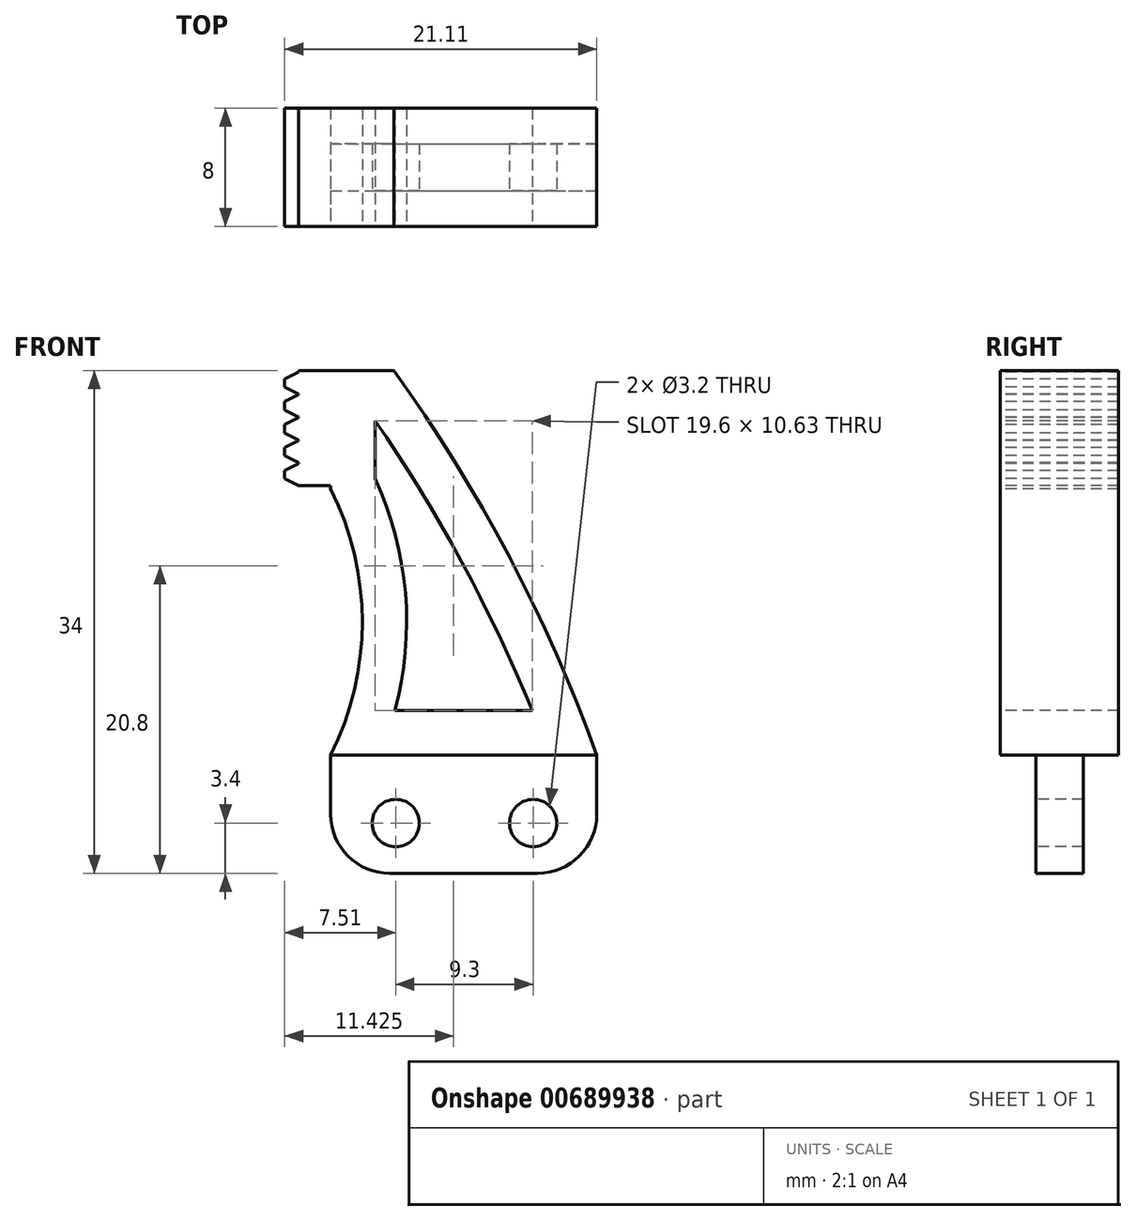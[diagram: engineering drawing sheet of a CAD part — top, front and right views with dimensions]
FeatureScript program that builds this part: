
annotation { "Feature Type Name" : "Feature", "Feature Type Description" : "" }
export const myFeature = defineFeature(function(context is Context, id is Id, definition is map)
    precondition{}
    {
        {
            var Q0;
            Q0=qCreatedBy(makeId("Front.planeOp"),FACE);
            var sketch = newSketch(context, id + "F0", { "sketchPlane" : qUnion([Q0])});
            skLineSegment(sketch, "E0.bottom", {"start": v(9, 15) * mm, "end": v(-9, 15) * mm});
            skLineSegment(sketch, "E0.left", {"start": v(9, 15) * mm, "end": v(9, -15) * mm});
            skLineSegment(sketch, "E0.right", {"start": v(-9, 15) * mm, "end": v(-9, -15) * mm});
            skPoint(sketch, "E0.middle", {"position": v(0, 0) * mm});
            skArc(sketch, "E1", {"start": v(-9, -11) * mm, "mid": v(-6.86, -2) * mm, "end": v(-9, 7) * mm});
            skArc(sketch, "E2", {"start": v(9, -11) * mm, "mid": v(3.04, 2.48) * mm, "end": v(-4.73, 15) * mm});
            skLineSegment(sketch, "E3", {"start": v(-11.16, 14.92) * mm, "end": v(-12.66, 14.17) * mm});
            skLineSegment(sketch, "E4", {"start": v(-11.16, 13.42) * mm, "end": v(-12.66, 14.17) * mm});
            skLineSegment(sketch, "E5.1.0.1", {"start": v(-11.16, 11.87) * mm, "end": v(-12.66, 12.62) * mm});
            skLineSegment(sketch, "E5.1.0.2", {"start": v(-11.16, 13.37) * mm, "end": v(-12.66, 12.62) * mm});
            skLineSegment(sketch, "E5.2.0.1", {"start": v(-11.16, 10.32) * mm, "end": v(-12.66, 11.07) * mm});
            skLineSegment(sketch, "E5.2.0.2", {"start": v(-11.16, 11.82) * mm, "end": v(-12.66, 11.07) * mm});
            skLineSegment(sketch, "E5.3.0.1", {"start": v(-11.16, 8.77) * mm, "end": v(-12.66, 9.52) * mm});
            skLineSegment(sketch, "E5.3.0.2", {"start": v(-11.16, 10.27) * mm, "end": v(-12.66, 9.52) * mm});
            skLineSegment(sketch, "E5.4.0.1", {"start": v(-11.16, 7.22) * mm, "end": v(-12.66, 7.97) * mm});
            skLineSegment(sketch, "E5.4.0.2", {"start": v(-11.16, 8.72) * mm, "end": v(-12.66, 7.97) * mm});
            skLineSegment(sketch, "E6", {"start": v(-9, -11) * mm, "end": v(9, -11) * mm});
            skLineSegment(sketch, "E7.top", {"start": v(-9, -19) * mm, "end": v(9, -19) * mm});
            skLineSegment(sketch, "E7.left", {"start": v(-9, -15) * mm, "end": v(-9, -19) * mm});
            skLineSegment(sketch, "E7.right", {"start": v(9, -15) * mm, "end": v(9, -19) * mm});
            skLineSegment(sketch, "E8.bottom", {"start": v(-9, 15) * mm, "end": v(-11.16, 15) * mm});
            skLineSegment(sketch, "E8.left", {"start": v(-9, 15) * mm, "end": v(-9, 7.22) * mm});
            skLineSegment(sketch, "E8.right", {"start": v(-11.16, 15) * mm, "end": v(-11.16, 7.22) * mm});
            skLineSegment(sketch, "E9.bottom", {"start": v(-9, 7) * mm, "end": v(-11.16, 7) * mm});
            skLineSegment(sketch, "E9.left", {"start": v(-9, 7) * mm, "end": v(-9, 7.22) * mm});
            skLineSegment(sketch, "E9.right", {"start": v(-11.16, 7) * mm, "end": v(-11.16, 7.22) * mm});
            skLineSegment(sketch, "E10", {"start": v(-11.16, 7.22) * mm, "end": v(-9, 7.22) * mm});
            skLineSegment(sketch, "E11", {"start": v(-12.11, 14.44) * mm, "end": v(-12.11, 7.7) * mm});
            skSolve(sketch);
        }
        {
            var Q0;
            {var subQ0=sQuery(id+"F0.wireOp",EDGE,"E11");var subQ1=sQuery(id+"F0.wireOp",EDGE,"E3");var subQ2=makeQuery(id+"F0.imprint","INTERSECT",VERTEX,{"derivedFrom":[subQ1,subQ0]});Q0=makeQuery(id+"F0.imprint","IMPRINT",FACE,{"disambiguationData":[TD([[makeQuery(id+"F0.imprint","IMPRINT",EDGE,{"disambiguationData":[TD([[subQ2,1.0]])],"derivedFrom":subQ1}),1.0]])]});}
            var Q1;
            {var subQ0=sQuery(id+"F0.wireOp",EDGE,"E11");var subQ1=sQuery(id+"F0.wireOp",EDGE,"E5.1.0.1");var subQ2=makeQuery(id+"F0.imprint","INTERSECT",VERTEX,{"derivedFrom":[subQ1,subQ0]});Q1=makeQuery(id+"F0.imprint","IMPRINT",FACE,{"disambiguationData":[TD([[makeQuery(id+"F0.imprint","IMPRINT",EDGE,{"disambiguationData":[TD([[subQ2,1.0]])],"derivedFrom":subQ1}),-1.0]])]});}
            var Q2;
            {var subQ8=sQuery(id+"F0.wireOp",EDGE,"E8.bottom");Q2=makeQuery(id+"F0.imprint","IMPRINT",FACE,{"disambiguationData":[TD([[makeQuery(id+"F0.imprint","IMPRINT",EDGE,{"derivedFrom":subQ8}),1.0]])]});}
            var Q3;
            Q3=makeQuery(id+"F0.imprint","IMPRINT",FACE,{"disambiguationData":[TD([[makeQuery(id+"F0.imprint","IMPRINT",EDGE,{"derivedFrom":sQuery(id+"F0.wireOp",EDGE,"E1")}),-1.0]])]});
            var Q4;
            {var subQ0=sQuery(id+"F0.wireOp",EDGE,"E11");var subQ1=sQuery(id+"F0.wireOp",EDGE,"E5.2.0.1");var subQ2=makeQuery(id+"F0.imprint","INTERSECT",VERTEX,{"derivedFrom":[subQ1,subQ0]});Q4=makeQuery(id+"F0.imprint","IMPRINT",FACE,{"disambiguationData":[TD([[makeQuery(id+"F0.imprint","IMPRINT",EDGE,{"disambiguationData":[TD([[subQ2,1.0]])],"derivedFrom":subQ1}),-1.0]])]});}
            var Q5;
            {var subQ0=sQuery(id+"F0.wireOp",EDGE,"E11");var subQ1=sQuery(id+"F0.wireOp",EDGE,"E5.3.0.1");var subQ2=makeQuery(id+"F0.imprint","INTERSECT",VERTEX,{"derivedFrom":[subQ1,subQ0]});Q5=makeQuery(id+"F0.imprint","IMPRINT",FACE,{"disambiguationData":[TD([[makeQuery(id+"F0.imprint","IMPRINT",EDGE,{"disambiguationData":[TD([[subQ2,1.0]])],"derivedFrom":subQ1}),-1.0]])]});}
            var Q6;
            {var subQ3=sQuery(id+"F0.wireOp",EDGE,"E11");var subQ5=sQuery(id+"F0.wireOp",EDGE,"E5.4.0.2");var subQ6=makeQuery(id+"F0.imprint","INTERSECT",VERTEX,{"derivedFrom":[subQ5,subQ3]});Q6=makeQuery(id+"F0.imprint","IMPRINT",FACE,{"disambiguationData":[TD([[makeQuery(id+"F0.imprint","IMPRINT",EDGE,{"disambiguationData":[TD([[subQ6,1.0]])],"derivedFrom":subQ5}),1.0]])]});}
            var Q7;
            {var subQ2=sQuery(id+"F0.wireOp",EDGE,"E6");Q7=makeQuery(id+"F0.imprint","IMPRINT",FACE,{"disambiguationData":[TD([[makeQuery(id+"F0.imprint","IMPRINT",EDGE,{"derivedFrom":subQ2}),-1.0]])]});}
            extrude(context, id + "F1", {"entities" : qUnion([Q0, Q1, Q2, Q3, Q4, Q5, Q6, Q7]), "oppositeDirection" : true, "depth" : 8 * mm, "offsetDistance" : 25 * mm});
        }
        {
            var Q0;
            Q0=makeQuery(id+"F1.opExtrude","CAP_FACE",FACE,{"disambiguationData":[OSD([sQuery(id+"F0.wireOp",EDGE,"E0.bottom"),sQuery(id+"F0.wireOp",EDGE,"E0.left"),sQuery(id+"F0.wireOp",EDGE,"E0.right"),sQuery(id+"F0.wireOp",EDGE,"E1"),sQuery(id+"F0.wireOp",EDGE,"E2"),sQuery(id+"F0.wireOp",EDGE,"E3"),sQuery(id+"F0.wireOp",EDGE,"E4"),sQuery(id+"F0.wireOp",EDGE,"E5.1.0.1"),sQuery(id+"F0.wireOp",EDGE,"E5.1.0.2"),sQuery(id+"F0.wireOp",EDGE,"E5.2.0.1"),sQuery(id+"F0.wireOp",EDGE,"E5.2.0.2"),sQuery(id+"F0.wireOp",EDGE,"E5.3.0.1"),sQuery(id+"F0.wireOp",EDGE,"E5.3.0.2"),sQuery(id+"F0.wireOp",EDGE,"E5.4.0.1"),sQuery(id+"F0.wireOp",EDGE,"E5.4.0.2"),sQuery(id+"F0.wireOp",EDGE,"ii1cAA1e-JSJr-z0bZ-yPhd-YXalWYOk9meH"),sQuery(id+"F0.wireOp",EDGE,"NeUnMBCx-EcG5-3TzF-d2Iy-VHdHwbOGnCjQ"),sQuery(id+"F0.wireOp",EDGE,"Bu8GrmuG-hVLc-6Zwb-ZN9j-FqlKQepw3AUV"),sQuery(id+"F0.wireOp",EDGE,"PhBtE8ru-nsp9-KEh6-Witq-BTG184TXn8xR"),sQuery(id+"F0.wireOp",EDGE,"dVbz5flj-GqEQ-BWn1-bWRb-yC5Nv96dNbSN"),sQuery(id+"F0.wireOp",EDGE,"E7.top"),sQuery(id+"F0.wireOp",EDGE,"E7.left"),sQuery(id+"F0.wireOp",EDGE,"E7.right")])],"isStart":false});
            var sketch = newSketch(context, id + "F2", { "sketchPlane" : qUnion([Q0])});
            skLineSegment(sketch, "E12", {"start": v(9, -11) * mm, "end": v(-9, -11) * mm});
            skSolve(sketch);
        }
        {
            var Q0;
            {var subQ2=sQuery(id+"F0.wireOp",EDGE,"E6");Q0=makeQuery(id+"F0.imprint","IMPRINT",FACE,{"disambiguationData":[TD([[makeQuery(id+"F0.imprint","IMPRINT",EDGE,{"derivedFrom":subQ2}),-1.0]])]});}
            extrude(context, id + "F3", {"entities" : qUnion([Q0]), "operationType" : NewBodyOperationType.REMOVE, "oppositeDirection" : true, "depth" : 2.4 * mm, "offsetDistance" : 25 * mm});
        }
        {
            var Q0;
            Q0=makeQuery(id+"F1.opExtrude","CAP_FACE",FACE,{"disambiguationData":[OSD([sQuery(id+"F0.wireOp",EDGE,"E0.bottom"),sQuery(id+"F0.wireOp",EDGE,"E0.left"),sQuery(id+"F0.wireOp",EDGE,"E0.right"),sQuery(id+"F0.wireOp",EDGE,"E1"),sQuery(id+"F0.wireOp",EDGE,"E2"),sQuery(id+"F0.wireOp",EDGE,"E3"),sQuery(id+"F0.wireOp",EDGE,"E4"),sQuery(id+"F0.wireOp",EDGE,"E5.1.0.1"),sQuery(id+"F0.wireOp",EDGE,"E5.1.0.2"),sQuery(id+"F0.wireOp",EDGE,"E5.2.0.1"),sQuery(id+"F0.wireOp",EDGE,"E5.2.0.2"),sQuery(id+"F0.wireOp",EDGE,"E5.3.0.1"),sQuery(id+"F0.wireOp",EDGE,"E5.3.0.2"),sQuery(id+"F0.wireOp",EDGE,"E5.4.0.1"),sQuery(id+"F0.wireOp",EDGE,"E5.4.0.2"),sQuery(id+"F0.wireOp",EDGE,"ii1cAA1e-JSJr-z0bZ-yPhd-YXalWYOk9meH"),sQuery(id+"F0.wireOp",EDGE,"NeUnMBCx-EcG5-3TzF-d2Iy-VHdHwbOGnCjQ"),sQuery(id+"F0.wireOp",EDGE,"Bu8GrmuG-hVLc-6Zwb-ZN9j-FqlKQepw3AUV"),sQuery(id+"F0.wireOp",EDGE,"PhBtE8ru-nsp9-KEh6-Witq-BTG184TXn8xR"),sQuery(id+"F0.wireOp",EDGE,"dVbz5flj-GqEQ-BWn1-bWRb-yC5Nv96dNbSN"),sQuery(id+"F0.wireOp",EDGE,"E7.top"),sQuery(id+"F0.wireOp",EDGE,"E7.left"),sQuery(id+"F0.wireOp",EDGE,"E7.right")])],"isStart":true});
            var sketch = newSketch(context, id + "F4", { "sketchPlane" : qUnion([Q0])});
            skLineSegment(sketch, "E13", {"start": v(-9, -11) * mm, "end": v(9, -11) * mm});
            skSolve(sketch);
        }
        {
            var Q0;
            Q0=makeQuery(id+"F2.imprint","IMPRINT",FACE,{"disambiguationData":[TD([[makeQuery(id+"F2.imprint","IMPRINT",EDGE,{"derivedFrom":sQuery(id+"F2.wireOp",EDGE,"E12")}),1.0]])]});
            extrude(context, id + "F5", {"entities" : qUnion([Q0]), "operationType" : NewBodyOperationType.REMOVE, "oppositeDirection" : true, "depth" : 2.4 * mm, "offsetDistance" : 25 * mm});
        }
        {
            var Q0;
            Q0=makeQuery(id+"F4.imprint","IMPRINT",FACE,{"disambiguationData":[TD([[makeQuery(id+"F4.imprint","IMPRINT",EDGE,{"derivedFrom":sQuery(id+"F4.wireOp",EDGE,"E13")}),1.0]])]});
            var sketch = newSketch(context, id + "F6", { "sketchPlane" : qUnion([Q0])});
            skArc(sketch, "E14.0", {"start": v(-9, -11) * mm, "mid": v(-6.86, -2) * mm, "end": v(-9, 7) * mm});
            skArc(sketch, "E15.0", {"start": v(9, -11) * mm, "mid": v(3.04, 2.48) * mm, "end": v(-4.73, 15) * mm});
            skLineSegment(sketch, "E16.0", {"start": v(-9, -11) * mm, "end": v(9, -11) * mm});
            skLineSegment(sketch, "E17.0", {"start": v(-4.73, 15) * mm, "end": v(-11.16, 15) * mm});
            skLineSegment(sketch, "E18", {"start": v(-9, 7) * mm, "end": v(-9, 15) * mm});
            skLineSegment(sketch, "E19.0", {"start": v(-6, 7.69) * mm, "end": v(-6, 15) * mm});
            skArc(sketch, "E19.1", {"start": v(-4.66, -8) * mm, "mid": v(-3.94, -0.04) * mm, "end": v(-6, 7.69) * mm});
            skLineSegment(sketch, "E19.2", {"start": v(-4.66, -8) * mm, "end": v(4.63, -8) * mm});
            skArc(sketch, "E19.3", {"start": v(4.63, -8) * mm, "mid": v(-0.64, 2.97) * mm, "end": v(-7.16, 13.25) * mm});
            skSolve(sketch);
        }
        {
            var Q0;
            {var subQ0=sQuery(id+"F6.wireOp",EDGE,"E19.1");Q0=makeQuery(id+"F6.imprint","IMPRINT",FACE,{"disambiguationData":[TD([[makeQuery(id+"F6.imprint","IMPRINT",EDGE,{"derivedFrom":subQ0}),-1.0]])]});}
            extrude(context, id + "F7", {"entities" : qUnion([Q0]), "operationType" : NewBodyOperationType.REMOVE, "oppositeDirection" : true, "depth" : 25 * mm, "offsetDistance" : 25 * mm});
        }
        {
            var Q0;
            Q0=makeQuery(id+"F3.boolean.opBoolean","COPY",FACE,{"derivedFrom":makeQuery(id+"F3.opExtrude","CAP_FACE",FACE,{"disambiguationData":[OSD([sQuery(id+"F0.wireOp",EDGE,"E0.left"),sQuery(id+"F0.wireOp",EDGE,"E0.right"),sQuery(id+"F0.wireOp",EDGE,"E6"),sQuery(id+"F0.wireOp",EDGE,"E7.top"),sQuery(id+"F0.wireOp",EDGE,"E7.left"),sQuery(id+"F0.wireOp",EDGE,"E7.right")])],"isStart":false})});
            var sketch = newSketch(context, id + "F8", { "sketchPlane" : qUnion([Q0])});
            skCircle(sketch, "E20", {"center": v(-4.6, -15.6) * mm, "radius": 1.6 * mm});
            skCircle(sketch, "E21", {"center": v(4.7, -15.6) * mm, "radius": 1.6 * mm});
            skPoint(sketch, "E22.orphan", {"position": v(9, -15) * mm});
            skPoint(sketch, "E23.start.orphan", {"position": v(-9, -15) * mm});
            skSolve(sketch);
        }
        {
            var Q0;
            Q0=makeQuery(id+"F8.imprint","IMPRINT",FACE,{"disambiguationData":[TD([[makeQuery(id+"F8.imprint","IMPRINT",EDGE,{"derivedFrom":sQuery(id+"F8.wireOp",EDGE,"E20")}),1.0]])]});
            var Q1;
            Q1=makeQuery(id+"F8.imprint","IMPRINT",FACE,{"disambiguationData":[TD([[makeQuery(id+"F8.imprint","IMPRINT",EDGE,{"derivedFrom":sQuery(id+"F8.wireOp",EDGE,"E21")}),1.0]])]});
            extrude(context, id + "F9", {"entities" : qUnion([Q0, Q1]), "operationType" : NewBodyOperationType.REMOVE, "oppositeDirection" : true, "depth" : 25 * mm, "offsetDistance" : 25 * mm});
        }
        {
            var Q0;
            Q0=makeQuery(id+"F1.opExtrude","SWEPT_EDGE",EDGE,{"disambiguationData":[OSD([sQuery(id+"F0.wireOp",EDGE,"E7.top"),sQuery(id+"F0.wireOp",EDGE,"E7.left")])]});
            var Q1;
            Q1=makeQuery(id+"F1.opExtrude","SWEPT_EDGE",EDGE,{"disambiguationData":[OSD([sQuery(id+"F0.wireOp",EDGE,"E7.top"),sQuery(id+"F0.wireOp",EDGE,"E7.right")])]});
            fillet(context, id + "F10", {"entities" : qUnion([Q0, Q1]), "radius" : 4 * mm, "tangentPropagation" : true, "allowEdgeOverflow" : false});
        }
    });
